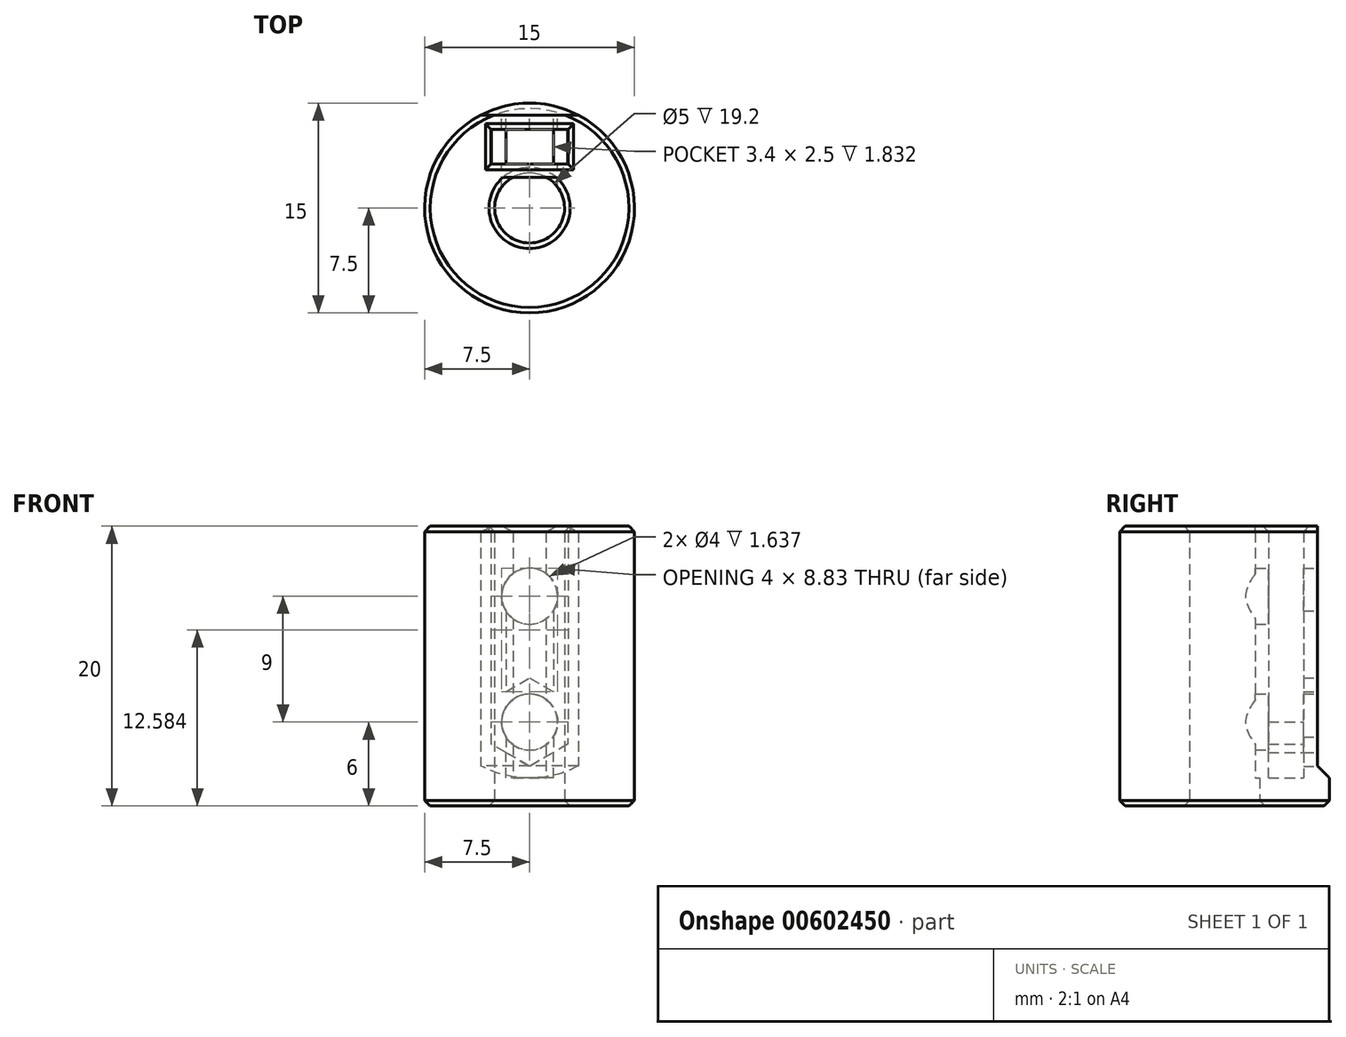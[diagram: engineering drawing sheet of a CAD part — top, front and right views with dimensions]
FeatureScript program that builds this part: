
annotation { "Feature Type Name" : "Feature", "Feature Type Description" : "" }
export const myFeature = defineFeature(function(context is Context, id is Id, definition is map)
    precondition{}
    {
        {
            var Q0;
            Q0=qCreatedBy(makeId("Top.planeOp"),FACE);
            var sketch = newSketch(context, id + "F0", { "sketchPlane" : qUnion([Q0])});
            skCircle(sketch, "E0", {"center": v(0, 0) * mm, "radius": 2.5 * mm});
            skCircle(sketch, "E1", {"center": v(0, 0) * mm, "radius": 7.5 * mm});
            skLineSegment(sketch, "E2", {"start": v(-1.19, 2.2) * mm, "end": v(1.19, 2.2) * mm});
            skLineSegment(sketch, "E3", {"start": v(-3.5, 6.63) * mm, "end": v(3.5, 6.63) * mm});
            skSolve(sketch);
        }
        {
            var Q0;
            {var subQ4=sQuery(id+"F0.wireOp",EDGE,"E3");Q0=makeQuery(id+"F0.imprint","IMPRINT",FACE,{"disambiguationData":[TD([[makeQuery(id+"F0.imprint","IMPRINT",EDGE,{"derivedFrom":subQ4}),-1.0]])]});}
            var Q1;
            {var subQ0=sQuery(id+"F0.wireOp",EDGE,"E3");Q1=makeQuery(id+"F0.imprint","IMPRINT",FACE,{"disambiguationData":[TD([[makeQuery(id+"F0.imprint","IMPRINT",EDGE,{"derivedFrom":subQ0}),1.0]])]});}
            extrude(context, id + "F1", {"entities" : qUnion([Q0, Q1]), "depth" : 2 * mm, "offsetDistance" : 25 * mm});
        }
        {
            var Q0;
            Q0=makeQuery(id+"F1.opExtrude","CAP_FACE",FACE,{"disambiguationData":[OSD([sQuery(id+"F0.wireOp",EDGE,"E0"),sQuery(id+"F0.wireOp",EDGE,"E1")])],"isStart":false});
            var sketch = newSketch(context, id + "F2", { "sketchPlane" : qUnion([Q0])});
            skCircle(sketch, "E4.0", {"center": v(0, 0) * mm, "radius": 2.5 * mm});
            skCircle(sketch, "E4.1", {"center": v(0, 0) * mm, "radius": 7.5 * mm});
            skLineSegment(sketch, "E4.2", {"start": v(-1.19, 2.2) * mm, "end": v(1.19, 2.2) * mm});
            skLineSegment(sketch, "E4.3", {"start": v(-3.5, 6.63) * mm, "end": v(3.5, 6.63) * mm});
            skLineSegment(sketch, "E5.bottom", {"start": v(2.75, 5.63) * mm, "end": v(-2.75, 5.63) * mm});
            skLineSegment(sketch, "E5.top", {"start": v(2.75, 3.13) * mm, "end": v(-2.75, 3.13) * mm});
            skLineSegment(sketch, "E5.left", {"start": v(2.75, 5.63) * mm, "end": v(2.75, 3.13) * mm});
            skLineSegment(sketch, "E5.right", {"start": v(-2.75, 5.63) * mm, "end": v(-2.75, 3.13) * mm});
            skPoint(sketch, "E5.middle", {"position": v(0, 4.38) * mm});
            skSolve(sketch);
        }
        {
            var Q0;
            {var subQ4=sQuery(id+"F2.wireOp",EDGE,"E4.3");Q0=makeQuery(id+"F2.imprint","IMPRINT",FACE,{"disambiguationData":[TD([[makeQuery(id+"F2.imprint","IMPRINT",EDGE,{"derivedFrom":subQ4}),-1.0]])]});}
            var Q1;
            {var subQ0=sQuery(id+"F2.wireOp",EDGE,"E4.2");Q1=makeQuery(id+"F2.imprint","IMPRINT",FACE,{"disambiguationData":[TD([[makeQuery(id+"F2.imprint","IMPRINT",EDGE,{"derivedFrom":subQ0}),1.0]])]});}
            extrude(context, id + "F3", {"entities" : qUnion([Q0, Q1]), "operationType" : NewBodyOperationType.ADD, "depth" : 18 * mm, "offsetDistance" : 25 * mm});
        }
        {
            var Q0;
            Q0=makeQuery(id+"F3.opExtrude","CAP_FACE",FACE,{"disambiguationData":[OSD([sQuery(id+"F2.wireOp",EDGE,"E4.0"),sQuery(id+"F2.wireOp",EDGE,"E4.1"),sQuery(id+"F2.wireOp",EDGE,"E4.2")])],"isStart":false});
            var sketch = newSketch(context, id + "F4", { "sketchPlane" : qUnion([Q0])});
            skCircle(sketch, "E6.0", {"center": v(0, 0) * mm, "radius": 7.5 * mm});
            skCircle(sketch, "E7.0", {"center": v(0, 0) * mm, "radius": 2.5 * mm});
            skCircle(sketch, "E8", {"center": v(0, 0) * mm, "radius": 4.5 * mm});
            skLineSegment(sketch, "E9", {"start": v(0, 4.5) * mm, "end": v(0, 7.5) * mm});
            skPoint(sketch, "E9.startSnap0", {"position": v(0, 6.63) * mm});
            skLineSegment(sketch, "E10", {"start": v(1.5, 4.24) * mm, "end": v(1.5, 7.35) * mm});
            skLineSegment(sketch, "E11", {"start": v(-1.5, 4.24) * mm, "end": v(-1.5, 7.35) * mm});
            skLineSegment(sketch, "E12.1.0", {"start": v(4.24, 1.5) * mm, "end": v(7.35, 1.5) * mm});
            skLineSegment(sketch, "E12.1.1", {"start": v(4.5, 0) * mm, "end": v(7.5, 0) * mm});
            skLineSegment(sketch, "E12.1.2", {"start": v(4.24, -1.5) * mm, "end": v(7.35, -1.5) * mm});
            skLineSegment(sketch, "E12.2.0", {"start": v(1.5, -4.24) * mm, "end": v(1.5, -7.35) * mm});
            skLineSegment(sketch, "E12.2.1", {"start": v(0, -4.5) * mm, "end": v(0, -7.5) * mm});
            skLineSegment(sketch, "E12.2.2", {"start": v(-1.5, -4.24) * mm, "end": v(-1.5, -7.35) * mm});
            skLineSegment(sketch, "E12.3.0", {"start": v(-4.24, -1.5) * mm, "end": v(-7.35, -1.5) * mm});
            skLineSegment(sketch, "E12.3.1", {"start": v(-4.5, 0) * mm, "end": v(-7.5, 0) * mm});
            skLineSegment(sketch, "E12.3.2", {"start": v(-4.24, 1.5) * mm, "end": v(-7.35, 1.5) * mm});
            skLineSegment(sketch, "E12.anchor1", {"start": v(0, 0) * mm, "end": v(-1.5, 4.24) * mm, "construction": true});
            skLineSegment(sketch, "E12.anchor2", {"start": v(0, 0) * mm, "end": v(-4.24, -1.5) * mm, "construction": true});
            skSolve(sketch);
        }
        {
            var Q0;
            Q0=makeQuery(id+"F3.opExtrude","SWEPT_FACE",FACE,{"disambiguationData":[OSD([sQuery(id+"F2.wireOp",EDGE,"E4.3")])]});
            var sketch = newSketch(context, id + "F5", { "sketchPlane" : qUnion([Q0])});
            skLineSegment(sketch, "E13.0", {"start": v(-7.5, 2) * mm, "end": v(7.5, 2) * mm});
            skLineSegment(sketch, "E14.0", {"start": v(3.5, 20) * mm, "end": v(3.5, 2) * mm});
            skLineSegment(sketch, "E15.0", {"start": v(-3.5, 20) * mm, "end": v(-3.5, 2) * mm});
            skLineSegment(sketch, "E16.0", {"start": v(-4.5, 20) * mm, "end": v(4.5, 20) * mm});
            skPoint(sketch, "E17", {"position": v(0, 6) * mm});
            skLineSegment(sketch, "E18", {"start": v(-3.5, 6) * mm, "end": v(3.5, 6) * mm});
            skLineSegment(sketch, "E19.bottom", {"start": v(1.7, 2) * mm, "end": v(-1.7, 2) * mm});
            skLineSegment(sketch, "E19.top", {"start": v(1.7, 20) * mm, "end": v(-1.7, 20) * mm});
            skLineSegment(sketch, "E19.left", {"start": v(1.7, 2) * mm, "end": v(1.7, 20) * mm});
            skLineSegment(sketch, "E19.right", {"start": v(-1.7, 2) * mm, "end": v(-1.7, 20) * mm});
            skCircle(sketch, "E20", {"center": v(0, 6) * mm, "radius": 2 * mm});
            skLineSegment(sketch, "E21", {"start": v(-3.5, 15) * mm, "end": v(3.5, 15) * mm});
            skCircle(sketch, "E22", {"center": v(0, 15) * mm, "radius": 2 * mm});
            skCircle(sketch, "E23.cCircle", {"center": v(0, 6) * mm, "radius": 3.15 * mm, "construction": true});
            skLineSegment(sketch, "E23.0", {"start": v(-2.73, 4.42) * mm, "end": v(-2.73, 7.58) * mm});
            skLineSegment(sketch, "E23.1", {"start": v(-2.73, 7.58) * mm, "end": v(0, 9.15) * mm});
            skLineSegment(sketch, "E23.2", {"start": v(0, 9.15) * mm, "end": v(2.73, 7.58) * mm});
            skLineSegment(sketch, "E23.3", {"start": v(2.73, 7.57) * mm, "end": v(2.73, 4.42) * mm});
            skLineSegment(sketch, "E23.4", {"start": v(2.73, 4.42) * mm, "end": v(0, 2.85) * mm});
            skLineSegment(sketch, "E23.5", {"start": v(0, 2.85) * mm, "end": v(-2.73, 4.43) * mm});
            skSolve(sketch);
        }
        {
            var Q0;
            {var subQ0=sQuery(id+"F5.wireOp",EDGE,"E19.top");Q0=makeQuery(id+"F5.imprint","IMPRINT",FACE,{"disambiguationData":[TD([[makeQuery(id+"F5.imprint","IMPRINT",EDGE,{"derivedFrom":subQ0}),1.0]])]});}
            var Q1;
            {var subQ0=sQuery(id+"F5.wireOp",EDGE,"E19.bottom");Q1=makeQuery(id+"F5.imprint","IMPRINT",FACE,{"disambiguationData":[TD([[makeQuery(id+"F5.imprint","IMPRINT",EDGE,{"derivedFrom":subQ0}),-1.0]])]});}
            var Q2;
            {var subQ0=sQuery(id+"F5.wireOp",EDGE,"E22");var subQ1=sQuery(id+"F5.wireOp",EDGE,"E19.left");var subQ2=makeQuery(id+"F5.imprint","INTERSECT",VERTEX,{"disambiguationData":[OD(0.0)],"derivedFrom":[subQ1,subQ0]});Q2=makeQuery(id+"F5.imprint","IMPRINT",FACE,{"disambiguationData":[TD([[makeQuery(id+"F5.imprint","IMPRINT",EDGE,{"disambiguationData":[TD([[subQ2,-1.0]])],"derivedFrom":subQ1}),1.0]])]});}
            var Q3;
            {var subQ0=sQuery(id+"F5.wireOp",EDGE,"E22");var subQ1=sQuery(id+"F5.wireOp",EDGE,"E19.right");var subQ2=makeQuery(id+"F5.imprint","INTERSECT",VERTEX,{"disambiguationData":[OD(0.0)],"derivedFrom":[subQ1,subQ0]});Q3=makeQuery(id+"F5.imprint","IMPRINT",FACE,{"disambiguationData":[TD([[makeQuery(id+"F5.imprint","IMPRINT",EDGE,{"disambiguationData":[TD([[subQ2,-1.0]])],"derivedFrom":subQ1}),1.0]])]});}
            var Q4;
            {var subQ0=sQuery(id+"F5.wireOp",EDGE,"E21");var subQ1=sQuery(id+"F5.wireOp",EDGE,"E19.right");var subQ2=makeQuery(id+"F5.imprint","INTERSECT",VERTEX,{"derivedFrom":[subQ1,subQ0]});Q4=makeQuery(id+"F5.imprint","IMPRINT",FACE,{"disambiguationData":[TD([[makeQuery(id+"F5.imprint","IMPRINT",EDGE,{"disambiguationData":[TD([[subQ2,-1.0]])],"derivedFrom":subQ1}),1.0]])]});}
            var Q5;
            {var subQ0=sQuery(id+"F5.wireOp",EDGE,"E21");var subQ1=sQuery(id+"F5.wireOp",EDGE,"E19.left");var subQ2=makeQuery(id+"F5.imprint","INTERSECT",VERTEX,{"derivedFrom":[subQ1,subQ0]});Q5=makeQuery(id+"F5.imprint","IMPRINT",FACE,{"disambiguationData":[TD([[makeQuery(id+"F5.imprint","IMPRINT",EDGE,{"disambiguationData":[TD([[subQ2,-1.0]])],"derivedFrom":subQ1}),-1.0]])]});}
            var Q6;
            {var subQ0=sQuery(id+"F5.wireOp",EDGE,"E22");var subQ1=sQuery(id+"F5.wireOp",EDGE,"E19.left");var subQ2=makeQuery(id+"F5.imprint","INTERSECT",VERTEX,{"disambiguationData":[OD(0.0)],"derivedFrom":[subQ1,subQ0]});Q6=makeQuery(id+"F5.imprint","IMPRINT",FACE,{"disambiguationData":[TD([[makeQuery(id+"F5.imprint","IMPRINT",EDGE,{"disambiguationData":[TD([[subQ2,-1.0]])],"derivedFrom":subQ1}),-1.0]])]});}
            var Q7;
            {var subQ0=sQuery(id+"F5.wireOp",EDGE,"E21");var subQ1=sQuery(id+"F5.wireOp",EDGE,"E19.left");var subQ2=makeQuery(id+"F5.imprint","INTERSECT",VERTEX,{"derivedFrom":[subQ1,subQ0]});Q7=makeQuery(id+"F5.imprint","IMPRINT",FACE,{"disambiguationData":[TD([[makeQuery(id+"F5.imprint","IMPRINT",EDGE,{"disambiguationData":[TD([[subQ2,-1.0]])],"derivedFrom":subQ1}),1.0]])]});}
            var Q8;
            {var subQ0=sQuery(id+"F5.wireOp",EDGE,"E19.right");var subQ1=sQuery(id+"F5.wireOp",EDGE,"E18");var subQ2=makeQuery(id+"F5.imprint","INTERSECT",VERTEX,{"derivedFrom":[subQ1,subQ0]});Q8=makeQuery(id+"F5.imprint","IMPRINT",FACE,{"disambiguationData":[TD([[makeQuery(id+"F5.imprint","IMPRINT",EDGE,{"disambiguationData":[TD([[subQ2,-1.0]])],"derivedFrom":subQ1}),-1.0]])]});}
            var Q9;
            {var subQ0=sQuery(id+"F5.wireOp",EDGE,"E20");var subQ1=sQuery(id+"F5.wireOp",EDGE,"E18");var subQ2=makeQuery(id+"F5.imprint","INTERSECT",VERTEX,{"disambiguationData":[OD(0.0)],"derivedFrom":[subQ1,subQ0]});Q9=makeQuery(id+"F5.imprint","IMPRINT",FACE,{"disambiguationData":[TD([[makeQuery(id+"F5.imprint","IMPRINT",EDGE,{"disambiguationData":[TD([[subQ2,-1.0]])],"derivedFrom":subQ1}),-1.0]])]});}
            var Q10;
            {var subQ0=sQuery(id+"F5.wireOp",EDGE,"E19.right");var subQ1=sQuery(id+"F5.wireOp",EDGE,"E18");var subQ2=makeQuery(id+"F5.imprint","INTERSECT",VERTEX,{"derivedFrom":[subQ1,subQ0]});Q10=makeQuery(id+"F5.imprint","IMPRINT",FACE,{"disambiguationData":[TD([[makeQuery(id+"F5.imprint","IMPRINT",EDGE,{"disambiguationData":[TD([[subQ2,-1.0]])],"derivedFrom":subQ1}),1.0]])]});}
            var Q11;
            {var subQ0=sQuery(id+"F5.wireOp",EDGE,"E19.left");var subQ1=sQuery(id+"F5.wireOp",EDGE,"E18");var subQ2=makeQuery(id+"F5.imprint","INTERSECT",VERTEX,{"derivedFrom":[subQ1,subQ0]});Q11=makeQuery(id+"F5.imprint","IMPRINT",FACE,{"disambiguationData":[TD([[makeQuery(id+"F5.imprint","IMPRINT",EDGE,{"disambiguationData":[TD([[subQ2,-1.0]])],"derivedFrom":subQ1}),1.0]])]});}
            var Q12;
            {var subQ0=sQuery(id+"F5.wireOp",EDGE,"E19.left");var subQ1=sQuery(id+"F5.wireOp",EDGE,"E18");var subQ2=makeQuery(id+"F5.imprint","INTERSECT",VERTEX,{"derivedFrom":[subQ1,subQ0]});Q12=makeQuery(id+"F5.imprint","IMPRINT",FACE,{"disambiguationData":[TD([[makeQuery(id+"F5.imprint","IMPRINT",EDGE,{"disambiguationData":[TD([[subQ2,-1.0]])],"derivedFrom":subQ1}),-1.0]])]});}
            var Q13;
            {var subQ0=sQuery(id+"F5.wireOp",EDGE,"E20");var subQ1=sQuery(id+"F5.wireOp",EDGE,"E18");var subQ2=makeQuery(id+"F5.imprint","INTERSECT",VERTEX,{"disambiguationData":[OD(0.0)],"derivedFrom":[subQ1,subQ0]});Q13=makeQuery(id+"F5.imprint","IMPRINT",FACE,{"disambiguationData":[TD([[makeQuery(id+"F5.imprint","IMPRINT",EDGE,{"disambiguationData":[TD([[subQ2,-1.0]])],"derivedFrom":subQ1}),1.0]])]});}
            var Q14;
            {var subQ1=sQuery(id+"F5.wireOp",EDGE,"E23.4");var subQ3=sQuery(id+"F5.wireOp",EDGE,"E19.left");var subQ4=makeQuery(id+"F5.imprint","INTERSECT",VERTEX,{"derivedFrom":[subQ3,subQ1]});Q14=makeQuery(id+"F5.imprint","IMPRINT",FACE,{"disambiguationData":[TD([[makeQuery(id+"F5.imprint","IMPRINT",EDGE,{"disambiguationData":[TD([[subQ4,-1.0]])],"derivedFrom":subQ3}),1.0]])]});}
            var Q15;
            {var subQ0=sQuery(id+"F5.wireOp",EDGE,"E23.2");var subQ5=sQuery(id+"F5.wireOp",EDGE,"E19.left");var subQ6=makeQuery(id+"F5.imprint","INTERSECT",VERTEX,{"derivedFrom":[subQ5,subQ0]});Q15=makeQuery(id+"F5.imprint","IMPRINT",FACE,{"disambiguationData":[TD([[makeQuery(id+"F5.imprint","IMPRINT",EDGE,{"disambiguationData":[TD([[subQ6,-1.0]])],"derivedFrom":subQ5}),1.0]])]});}
            var Q16;
            {var subQ5=sQuery(id+"F5.wireOp",EDGE,"E20");var subQ7=sQuery(id+"F5.wireOp",EDGE,"E19.left");var subQ8=makeQuery(id+"F5.imprint","INTERSECT",VERTEX,{"disambiguationData":[OD(1.0)],"derivedFrom":[subQ7,subQ5]});Q16=makeQuery(id+"F5.imprint","IMPRINT",FACE,{"disambiguationData":[TD([[makeQuery(id+"F5.imprint","IMPRINT",EDGE,{"disambiguationData":[TD([[subQ8,-1.0]])],"derivedFrom":subQ7}),1.0]])]});}
            extrude(context, id + "F6", {"entities" : qUnion([Q0, Q1, Q2, Q3, Q4, Q5, Q6, Q7, Q8, Q9, Q10, Q11, Q12, Q13, Q14, Q15, Q16]), "operationType" : NewBodyOperationType.REMOVE, "oppositeDirection" : true, "depth" : 1.34 * mm, "offsetDistance" : 25 * mm});
        }
        {
            var Q0;
            Q0=sQuery(id+"F5.wireOp",VERTEX,"E17");
            var Q1;
            Q1=sQuery(id+"F5.wireOp",VERTEX,"E22.center");
            var Q2;
            Q2=makeQuery(id+"F1.opExtrude","SWEPT_BODY",BODY,{"disambiguationData":[OSD([sQuery(id+"F0.wireOp",EDGE,"E0"),sQuery(id+"F0.wireOp",EDGE,"E1")])]});
            hole(context, id + "F7", {"style" : HoleStyle.SIMPLE, "endStyle" : HoleEndStyle.BLIND, "holeDiameter" : 4 * mm, "majorDiameter" : 5 * mm, "holeDepth" : 4 * mm, "isTappedThrough" : true, "tappedDepth" : 12 * mm, "tapClearance" : 3, "locations" : qUnion([Q0, Q1]), "scope" : qUnion([Q2])});
        }
        {
            var Q0;
            {var subQ1=sQuery(id+"F5.wireOp",EDGE,"E13.0");var subQ6=sQuery(id+"F5.wireOp",EDGE,"E15.0");var subQ11=makeQuery(id+"F5.imprint","INTERSECT",VERTEX,{"derivedFrom":[subQ1,subQ6]});Q0=makeQuery(id+"F5.imprint","IMPRINT",FACE,{"disambiguationData":[TD([[makeQuery(id+"F5.imprint","IMPRINT",EDGE,{"disambiguationData":[TD([[subQ11,1.0]])],"derivedFrom":subQ6}),1.0]])]});}
            var Q1;
            {var subQ5=sQuery(id+"F5.wireOp",EDGE,"E19.bottom");Q1=makeQuery(id+"F5.imprint","IMPRINT",FACE,{"disambiguationData":[TD([[makeQuery(id+"F5.imprint","IMPRINT",EDGE,{"derivedFrom":subQ5}),-1.0]])]});}
            var Q2;
            {var subQ1=sQuery(id+"F5.wireOp",EDGE,"E14.0");var subQ6=sQuery(id+"F5.wireOp",EDGE,"E13.0");var subQ10=makeQuery(id+"F5.imprint","INTERSECT",VERTEX,{"derivedFrom":[subQ6,subQ1]});Q2=makeQuery(id+"F5.imprint","IMPRINT",FACE,{"disambiguationData":[TD([[makeQuery(id+"F5.imprint","IMPRINT",EDGE,{"disambiguationData":[TD([[subQ10,1.0]])],"derivedFrom":subQ1}),-1.0]])]});}
            extrude(context, id + "F8", {"entities" : qUnion([Q0, Q1, Q2]), "operationType" : NewBodyOperationType.ADD, "oppositeDirection" : true, "depth" : 3.5 * mm, "offsetDistance" : 25 * mm});
        }
        {
            var Q0;
            {var subQ0=sQuery(id+"F5.wireOp",EDGE,"E19.bottom");var subQ1=sQuery(id+"F5.wireOp",EDGE,"E13.0");var subQ3=sQuery(id+"F2.wireOp",EDGE,"E4.3");var subQ9=sQuery(id+"F5.wireOp",EDGE,"E19.right");var subQ10=makeQuery(id+"F5.imprint","INTERSECT",VERTEX,{"derivedFrom":[subQ9,sQuery(id+"F5.wireOp",EDGE,"E23.5")]});var subQ12=makeQuery(id+"F3.opExtrude","CAP_EDGE",EDGE,{"disambiguationData":[OSD([subQ3])],"isStart":true});var subQ13=sQuery(id+"F5.wireOp",EDGE,"E19.left");var subQ14=makeQuery(id+"F5.imprint","INTERSECT",VERTEX,{"derivedFrom":[subQ13,sQuery(id+"F5.wireOp",EDGE,"E23.4")]});Q0=makeQuery(id+"F8.boolean.opBoolean","MERGE",EDGE,{"derivedFrom":[makeQuery(id+"F6.boolean.opBoolean","SPLIT",EDGE,{"disambiguationData":[TD([makeQuery(id+"F6.opExtrude","SWEPT_FACE",FACE,{"disambiguationData":[OSD([subQ13]),TDD([makeQuery(id+"F5.imprint","IMPRINT",EDGE,{"disambiguationData":[TD([[subQ14,1.0]])],"derivedFrom":subQ13}),makeQuery(id+"F5.imprint","IMPRINT",EDGE,{"disambiguationData":[TD([[subQ14,-1.0]])],"derivedFrom":subQ13})])]})])],"derivedFrom":subQ12}),makeQuery(id+"F6.boolean.opBoolean","SPLIT",EDGE,{"disambiguationData":[TD([makeQuery(id+"F6.opExtrude","SWEPT_FACE",FACE,{"disambiguationData":[OSD([subQ9]),TDD([makeQuery(id+"F5.imprint","IMPRINT",EDGE,{"disambiguationData":[TD([[subQ10,1.0]])],"derivedFrom":subQ9}),makeQuery(id+"F5.imprint","IMPRINT",EDGE,{"disambiguationData":[TD([[subQ10,-1.0]])],"derivedFrom":subQ9})])]})])],"derivedFrom":subQ12}),makeQuery(id+"F8.opExtrude","CAP_EDGE",EDGE,{"disambiguationData":[OSD([subQ1,subQ0])],"isStart":true})]});}
            chamfer(context, id + "F9", {"entities" : qUnion([Q0]), "width" : 0.87 * mm, "tangentPropagation" : true});
        }
        {
            var Q0;
            Q0=makeQuery(id+"F1.opExtrude","CAP_EDGE",EDGE,{"disambiguationData":[OSD([sQuery(id+"F0.wireOp",EDGE,"E1")])],"isStart":true});
            var Q1;
            Q1=makeQuery(id+"F1.opExtrude","CAP_EDGE",EDGE,{"disambiguationData":[OSD([sQuery(id+"F0.wireOp",EDGE,"E0")])],"isStart":true});
            var Q2;
            Q2=makeQuery(id+"F3.opExtrude","CAP_EDGE",EDGE,{"disambiguationData":[OSD([sQuery(id+"F2.wireOp",EDGE,"E4.0")])],"isStart":false});
            var Q3;
            Q3=makeQuery(id+"F3.opExtrude","CAP_EDGE",EDGE,{"disambiguationData":[OSD([sQuery(id+"F2.wireOp",EDGE,"E4.1")])],"isStart":false});
            var Q4;
            Q4=makeQuery(id+"F3.opExtrude","CAP_EDGE",EDGE,{"disambiguationData":[OSD([sQuery(id+"F2.wireOp",EDGE,"E5.top")])],"isStart":false});
            var Q5;
            Q5=makeQuery(id+"F3.opExtrude","CAP_EDGE",EDGE,{"disambiguationData":[OSD([sQuery(id+"F2.wireOp",EDGE,"E5.left")])],"isStart":false});
            var Q6;
            {var subQ0=sQuery(id+"F2.wireOp",EDGE,"E5.left");var subQ1=sQuery(id+"F2.wireOp",EDGE,"E5.bottom");Q6=makeQuery(id+"F6.boolean.opBoolean","SPLIT",EDGE,{"disambiguationData":[TD([makeQuery(id+"F3.opExtrude","SWEPT_FACE",FACE,{"disambiguationData":[OSD([subQ0])]})])],"derivedFrom":makeQuery(id+"F3.opExtrude","CAP_EDGE",EDGE,{"disambiguationData":[OSD([subQ1])],"isStart":false})});}
            var Q7;
            {var subQ0=sQuery(id+"F2.wireOp",EDGE,"E5.right");var subQ1=sQuery(id+"F2.wireOp",EDGE,"E5.bottom");Q7=makeQuery(id+"F6.boolean.opBoolean","SPLIT",EDGE,{"disambiguationData":[TD([makeQuery(id+"F3.opExtrude","SWEPT_FACE",FACE,{"disambiguationData":[OSD([subQ0])]})])],"derivedFrom":makeQuery(id+"F3.opExtrude","CAP_EDGE",EDGE,{"disambiguationData":[OSD([subQ1])],"isStart":false})});}
            var Q8;
            Q8=makeQuery(id+"F3.opExtrude","CAP_EDGE",EDGE,{"disambiguationData":[OSD([sQuery(id+"F2.wireOp",EDGE,"E5.right")])],"isStart":false});
            chamfer(context, id + "F10", {"entities" : qUnion([Q0, Q1, Q2, Q3, Q4, Q5, Q6, Q7, Q8]), "width" : 0.4 * mm, "tangentPropagation" : true});
        }
    });
